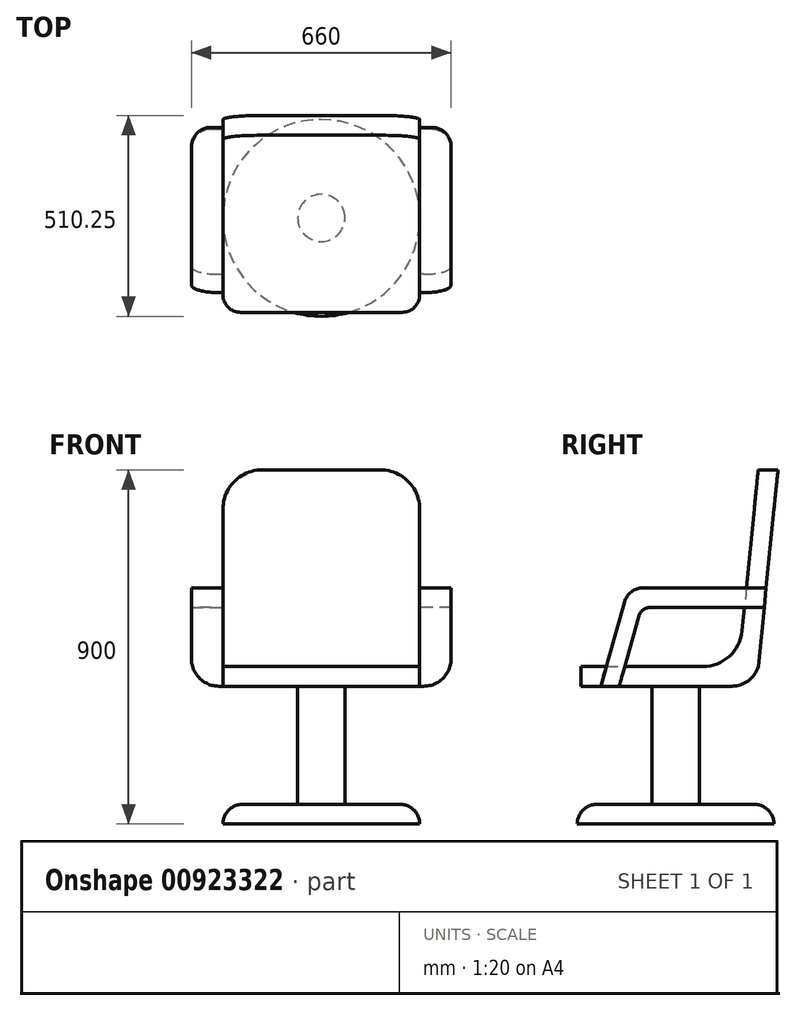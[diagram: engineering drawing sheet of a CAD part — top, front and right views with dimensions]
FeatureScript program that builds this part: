
annotation { "Feature Type Name" : "Feature", "Feature Type Description" : "" }
export const myFeature = defineFeature(function(context is Context, id is Id, definition is map)
    precondition{}
    {
        {
            var Q0;
            Q0=qCreatedBy(makeId("Top.planeOp"),FACE);
            var sketch = newSketch(context, id + "F0", { "sketchPlane" : qUnion([Q0])});
            skCircle(sketch, "E0", {"center": v(0, 0) * mm, "radius": 250 * mm});
            skSolve(sketch);
        }
        {
            var Q0;
            Q0 = qSketchRegion(id + "F0", true);
            extrude(context, id + "F1", {"entities" : qUnion([Q0]), "depth" : 50 * mm, "offsetDistance" : 25 * mm});
        }
        {
            var Q0;
            Q0=makeQuery(id+"F1.opExtrude","CAP_FACE",FACE,{"disambiguationData":[OSD([sQuery(id+"F0.wireOp",EDGE,"E0")])],"isStart":false});
            var sketch = newSketch(context, id + "F2", { "sketchPlane" : qUnion([Q0])});
            skCircle(sketch, "E1", {"center": v(0, 0) * mm, "radius": 60 * mm});
            skSolve(sketch);
        }
        {
            var Q0;
            Q0 = qSketchRegion(id + "F2", true);
            extrude(context, id + "F3", {"entities" : qUnion([Q0]), "operationType" : NewBodyOperationType.ADD, "depth" : (400 - 50 - 50) * mm, "offsetDistance" : 25 * mm});
        }
        {
            var Q0;
            Q0=qCreatedBy(makeId("Right.planeOp"),FACE);
            var sketch = newSketch(context, id + "F4", { "sketchPlane" : qUnion([Q0])});
            skLineSegment(sketch, "E2.bottom", {"start": v(-240, 400) * mm, "end": v(159.75, 400) * mm});
            skLineSegment(sketch, "E2.top", {"start": v(-240, 350) * mm, "end": v(210, 350) * mm});
            skLineSegment(sketch, "E2.left", {"start": v(-240, 400) * mm, "end": v(-240, 350) * mm});
            skLineSegment(sketch, "E2.right", {"start": v(210, 400) * mm, "end": v(210, 350) * mm});
            skLineSegment(sketch, "E3", {"start": v(210, 400) * mm, "end": v(260.25, 900) * mm});
            skLineSegment(sketch, "E4", {"start": v(260.25, 900) * mm, "end": v(210, 900) * mm});
            skLineSegment(sketch, "E5", {"start": v(210, 900) * mm, "end": v(159.75, 400) * mm});
            skLineSegment(sketch, "E6", {"start": v(0, 0) * mm, "end": v(0, 580.23) * mm, "construction": true});
            skSolve(sketch);
        }
        {
            var Q0;
            Q0 = qSketchRegion(id + "F4", true);
            extrude(context, id + "F5", {"entities" : qUnion([Q0]), "endBound" : BoundingType.SYMMETRIC, "depth" : 500 * mm, "offsetDistance" : 25 * mm});
        }
        {
            var Q0;
            Q0=makeQuery(id+"F5.opExtrude","CAP_FACE",FACE,{"disambiguationData":[OSD([sQuery(id+"F4.wireOp",EDGE,"E2.bottom"),sQuery(id+"F4.wireOp",EDGE,"E2.top"),sQuery(id+"F4.wireOp",EDGE,"E2.left"),sQuery(id+"F4.wireOp",EDGE,"E2.right"),sQuery(id+"F4.wireOp",EDGE,"E3"),sQuery(id+"F4.wireOp",EDGE,"E4"),sQuery(id+"F4.wireOp",EDGE,"E5")])],"isStart":false});
            var sketch = newSketch(context, id + "F6", { "sketchPlane" : qUnion([Q0])});
            skLineSegment(sketch, "E7", {"start": v(230.1, 600) * mm, "end": v(-119.9, 600) * mm});
            skLineSegment(sketch, "E8", {"start": v(-119.9, 600) * mm, "end": v(-190, 350) * mm});
            skLineSegment(sketch, "E9", {"start": v(-190, 350) * mm, "end": v(-143.26, 350) * mm});
            skLineSegment(sketch, "E10", {"start": v(-143.26, 350) * mm, "end": v(-87.18, 550) * mm});
            skLineSegment(sketch, "E11", {"start": v(-87.18, 550) * mm, "end": v(225.08, 550) * mm});
            skLineSegment(sketch, "E12", {"start": v(225.08, 550) * mm, "end": v(230.1, 600) * mm});
            skSolve(sketch);
        }
        {
            var Q0;
            {var subQ0=sQuery(id+"F6.wireOp",EDGE,"E12");Q0=makeQuery(id+"F6.imprint","IMPRINT",FACE,{"disambiguationData":[TD([[makeQuery(id+"F6.imprint","IMPRINT",EDGE,{"derivedFrom":subQ0}),1.0]])]});}
            var Q1;
            {var subQ0=sQuery(id+"F6.wireOp",EDGE,"E9");Q1=makeQuery(id+"F6.imprint","IMPRINT",FACE,{"disambiguationData":[TD([[makeQuery(id+"F6.imprint","IMPRINT",EDGE,{"derivedFrom":subQ0}),1.0]])]});}
            var Q2;
            {var subQ5=sQuery(id+"F6.wireOp",EDGE,"E8");var subQ6=sQuery(id+"F6.wireOp",EDGE,"E7");var subQ7=makeQuery(id+"F6.imprint","INTERSECT",VERTEX,{"derivedFrom":[subQ6,subQ5]});Q2=makeQuery(id+"F6.imprint","IMPRINT",FACE,{"disambiguationData":[TD([[makeQuery(id+"F6.imprint","IMPRINT",EDGE,{"disambiguationData":[TD([[subQ7,1.0]])],"derivedFrom":subQ6}),1.0]])]});}
            extrude(context, id + "F7", {"entities" : qUnion([Q0, Q1, Q2]), "depth" : 80 * mm, "offsetDistance" : 25 * mm});
        }
        {
            var Q0;
            Q0=makeQuery(id+"F7.opExtrude","SWEPT_BODY",BODY,{"disambiguationData":[OSD([sQuery(id+"F6.wireOp",EDGE,"E7"),sQuery(id+"F6.wireOp",EDGE,"E8"),sQuery(id+"F6.wireOp",EDGE,"E9"),sQuery(id+"F6.wireOp",EDGE,"E10"),sQuery(id+"F6.wireOp",EDGE,"E11"),sQuery(id+"F6.wireOp",EDGE,"E12")])]});
            var Q1;
            Q1=qCreatedBy(makeId("Right.planeOp"),FACE);
            mirror(context, id + "F8", {"operationType" : NewBodyOperationType.ADD, "entities" : qUnion([Q0]), "mirrorPlane" : qUnion([Q1])});
        }
        {
            var Q0;
            Q0=makeQuery(id+"F5.opExtrude","CAP_EDGE",EDGE,{"disambiguationData":[OSD([sQuery(id+"F4.wireOp",EDGE,"E2.left")])],"isStart":false});
            var Q1;
            Q1=makeQuery(id+"F5.opExtrude","CAP_EDGE",EDGE,{"disambiguationData":[OSD([sQuery(id+"F4.wireOp",EDGE,"E2.left")])],"isStart":true});
            fillet(context, id + "F9", {"entities" : qUnion([Q0, Q1]), "radius" : 45 * mm, "tangentPropagation" : true, "allowEdgeOverflow" : false});
        }
        {
            var Q0;
            Q0=makeQuery(id+"F5.opExtrude","CAP_EDGE",EDGE,{"disambiguationData":[OSD([sQuery(id+"F4.wireOp",EDGE,"E4")])],"isStart":false});
            var Q1;
            Q1=makeQuery(id+"F5.opExtrude","CAP_EDGE",EDGE,{"disambiguationData":[OSD([sQuery(id+"F4.wireOp",EDGE,"E4")])],"isStart":true});
            fillet(context, id + "F10", {"entities" : qUnion([Q0, Q1]), "radius" : 100 * mm, "tangentPropagation" : true, "allowEdgeOverflow" : false});
        }
        {
            var Q0;
            Q0=makeQuery(id+"F5.opExtrude","SWEPT_EDGE",EDGE,{"disambiguationData":[OSD([sQuery(id+"F4.wireOp",EDGE,"E2.bottom"),sQuery(id+"F4.wireOp",EDGE,"E5")])]});
            fillet(context, id + "F11", {"entities" : qUnion([Q0]), "radius" : 100 * mm, "tangentPropagation" : true, "allowEdgeOverflow" : false});
        }
        {
            var Q0;
            Q0=makeQuery(id+"F5.opExtrude","SWEPT_EDGE",EDGE,{"disambiguationData":[OSD([sQuery(id+"F4.wireOp",EDGE,"E2.top"),sQuery(id+"F4.wireOp",EDGE,"E2.right")])]});
            fillet(context, id + "F12", {"entities" : qUnion([Q0]), "radius" : 70 * mm, "tangentPropagation" : true, "allowEdgeOverflow" : false});
        }
        {
            var Q0;
            Q0=makeQuery(id+"F7.opExtrude","SWEPT_EDGE",EDGE,{"disambiguationData":[OSD([sQuery(id+"F6.wireOp",EDGE,"E7"),sQuery(id+"F6.wireOp",EDGE,"E8")])]});
            var Q1;
            Q1=makeQuery(id+"F8.opPattern","COPY",EDGE,{"derivedFrom":makeQuery(id+"F7.opExtrude","SWEPT_EDGE",EDGE,{"disambiguationData":[OSD([sQuery(id+"F6.wireOp",EDGE,"E7"),sQuery(id+"F6.wireOp",EDGE,"E8")])]}),"instanceName":"1"});
            fillet(context, id + "F13", {"entities" : qUnion([Q0, Q1]), "radius" : 50 * mm, "tangentPropagation" : true, "allowEdgeOverflow" : false});
        }
        {
            var Q0;
            Q0=makeQuery(id+"F7.opExtrude","SWEPT_EDGE",EDGE,{"disambiguationData":[OSD([sQuery(id+"F6.wireOp",EDGE,"E10"),sQuery(id+"F6.wireOp",EDGE,"E11")])]});
            var Q1;
            Q1=makeQuery(id+"F8.opPattern","COPY",EDGE,{"derivedFrom":makeQuery(id+"F7.opExtrude","SWEPT_EDGE",EDGE,{"disambiguationData":[OSD([sQuery(id+"F6.wireOp",EDGE,"E10"),sQuery(id+"F6.wireOp",EDGE,"E11")])]}),"instanceName":"1"});
            fillet(context, id + "F14", {"entities" : qUnion([Q0, Q1]), "radius" : 30 * mm, "tangentPropagation" : true, "allowEdgeOverflow" : false});
        }
        {
            var Q0;
            Q0=makeQuery(id+"F7.opExtrude","CAP_EDGE",EDGE,{"disambiguationData":[OSD([sQuery(id+"F6.wireOp",EDGE,"E9")])],"isStart":false});
            var Q1;
            Q1=makeQuery(id+"F8.opPattern","COPY",EDGE,{"derivedFrom":makeQuery(id+"F7.opExtrude","CAP_EDGE",EDGE,{"disambiguationData":[OSD([sQuery(id+"F6.wireOp",EDGE,"E9")])],"isStart":false}),"instanceName":"1"});
            fillet(context, id + "F15", {"entities" : qUnion([Q0, Q1]), "radius" : 70 * mm, "tangentPropagation" : true, "allowEdgeOverflow" : false});
        }
        {
            var Q0;
            Q0=makeQuery(id+"F7.opExtrude","CAP_EDGE",EDGE,{"disambiguationData":[OSD([sQuery(id+"F6.wireOp",EDGE,"E12")])],"isStart":false});
            var Q1;
            Q1=makeQuery(id+"F8.opPattern","COPY",EDGE,{"derivedFrom":makeQuery(id+"F7.opExtrude","CAP_EDGE",EDGE,{"disambiguationData":[OSD([sQuery(id+"F6.wireOp",EDGE,"E12")])],"isStart":false}),"instanceName":"1"});
            fillet(context, id + "F16", {"entities" : qUnion([Q0, Q1]), "radius" : 50 * mm, "tangentPropagation" : true, "allowEdgeOverflow" : false});
        }
        {
            var Q0;
            Q0=makeQuery(id+"F1.opExtrude","CAP_EDGE",EDGE,{"disambiguationData":[OSD([sQuery(id+"F0.wireOp",EDGE,"E0")])],"isStart":false});
            fillet(context, id + "F17", {"entities" : qUnion([Q0]), "radius" : 50 * mm, "tangentPropagation" : true, "allowEdgeOverflow" : false});
        }
    });
